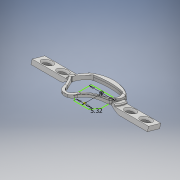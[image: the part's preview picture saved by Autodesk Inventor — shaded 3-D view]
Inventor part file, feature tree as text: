
AUTODESK INVENTOR PART (.ipt)
format: ipt  version: 2018 (Build 220112000, 112)  size: 2,529,280 bytes
history: native  units: mm
features: sketch x73, extrude x68, fillet x42, mirror x3, shell x1, hole x1
ambient origin geometry x8: Origin, YZ Plane, XZ Plane, XY Plane, X Axis, Y Axis, Z Axis, Center Point
bodies: Solid1 (feature_tree)
feature tree (188):
  extrude  "Extrusion1"  TaperAngle=0.0deg  [1 undecoded]
  extrude  "Extrusion2"  Depth=10.0mm
  extrude  "Extrusion3"  TaperAngle=0.0deg  [1 undecoded]
  shell  "Shell2"  Thickness=0.0mm
  extrude  "Extrusion4"  Depth=1.6mm
  extrude  "Extrusion6"  Depth=10.0mm TaperAngle=0.0deg
  extrude  "Extrusion7"  Depth=1.75mm
  extrude  "Extrusion8"  Depth=2.0mm
  extrude  "Extrusion9"  Depth=10.0mm TaperAngle=0.0deg
  extrude  "Extrusion11"  Depth=10.0mm TaperAngle=0.0deg
  fillet  "Fillet1"  Radius=10.0mm
  fillet  "Fillet2"  Radius=10.0mm
  fillet  "Fillet3"  [1 undecoded]
  fillet  "Fillet4"  Radius=0.541mm
  fillet  "Fillet5"  [1 undecoded]
  extrude  "Extrusion12"  Depth=7.5mm TaperAngle=0.0deg
  extrude  "Extrusion13"  TaperAngle=0.0deg  [1 undecoded]
  extrude  "Extrusion16"  Depth=51.0mm TaperAngle=0.0deg
  extrude  "Extrusion17"  TaperAngle=0.0deg  [1 undecoded]
  extrude  "Extrusion18"  Depth=10.0mm TaperAngle=0.0deg
  extrude  "Extrusion19"  Depth=10.0mm TaperAngle=0.0deg
  fillet  "Fillet6"  Radius=6.0mm
  extrude  "Extrusion20"  Depth=42.0mm TaperAngle=0.0deg
  fillet  "Fillet7"  Radius=42.0mm
  extrude  "Extrusion21"  Depth=2.6mm
  extrude  "Extrusion22"  Depth=2.6mm
  sketch  "Sketch23"  dims[d147=12.0125mm d148=12.0125mm]
  extrude  "Extrusion24"  Depth=12.0125mm
  extrude  "Extrusion26"  Depth=17.5mm
  extrude  "Extrusion28"  Depth=3.0mm
  extrude  "Extrusion32"  Depth=3.0mm
  extrude  "Extrusion37"  Depth=12.0mm TaperAngle=0.0deg
  extrude  "Extrusion38"  Depth=10.0mm TaperAngle=0.0deg
  extrude  "Extrusion40"  Depth=3.11mm
  extrude  "Extrusion41"  Depth=10.0mm TaperAngle=0.0deg
  extrude  "Extrusion42"  Depth=0.365mm TaperAngle=0.0deg
  extrude  "Extrusion43"  TaperAngle=0.0deg  [1 undecoded]
  extrude  "Extrusion44"  TaperAngle=0.0deg  [1 undecoded]
  hole  "Hole1"  [1 undecoded]
  sketch  "Sketch45"  dims[d203=20.0mm d204=15.65mm d205=0.0mm]
  extrude  "Extrusion45"  Depth=15.65mm TaperAngle=0.0deg
  extrude  "Extrusion47"  Depth=0.861mm
  mirror  "Mirror1"
  extrude  "Extrusion48"  Depth=1.61mm
  fillet  "Fillet23"  [1 undecoded]
  fillet  "Fillet24"  Radius=1.92mm
  extrude  "Extrusion49"  Depth=0.276mm
  extrude  "Extrusion50"  TaperAngle=0.0deg  [1 undecoded]
  extrude  "Extrusion54"  TaperAngle=0.0deg  [1 undecoded]
  extrude  "Extrusion55"  Depth=2.5mm
  extrude  "Extrusion56"  TaperAngle=0.0deg  [1 undecoded]
  extrude  "Extrusion57"  Depth=10.0mm TaperAngle=0.0deg
  sketch  "Sketch61"  dims[d255=2.57mm d256=2.37mm]
  extrude  "Extrusion58"  Depth=0.83mm TaperAngle=0.0deg
  extrude  "Extrusion59"  Depth=2.37mm
  extrude  "Extrusion60"  Depth=4.5mm
  fillet  "Fillet27"  Radius=0.83mm
  fillet  "Fillet28"  Radius=6.37mm
  extrude  "Extrusion61"  Depth=6.37mm TaperAngle=0.0deg
  fillet  "Fillet29"  Radius=6.71mm
  fillet  "Fillet30"  Radius=6.71mm
  fillet  "Fillet31"  [1 undecoded]
  fillet  "Fillet32"  Radius=2.0mm
  extrude  "Extrusion62"  Depth=2.0mm
  fillet  "Fillet33"  Radius=2.0mm
  fillet  "Fillet34"  Radius=2.0mm
  fillet  "Fillet35"  Radius=2.0mm
  fillet  "Fillet36"  Radius=2.0mm
  extrude  "Extrusion63"  Depth=1.9mm
  extrude  "Extrusion64"  Depth=0.616mm
  extrude  "Extrusion65"  Depth=2.0mm
  fillet  "Fillet37"  Radius=1.76mm
  fillet  "Fillet38"  [1 undecoded]
  extrude  "Extrusion69"  Depth=0.409mm
  extrude  "Extrusion70"  Depth=6.7mm TaperAngle=0.0deg
  extrude  "Extrusion71"  TaperAngle=0.0deg  [1 undecoded]
  extrude  "Extrusion72"  Depth=2.0mm
  extrude  "Extrusion73"  Depth=6.7mm TaperAngle=0.0deg
  extrude  "Extrusion74"  Depth=0.241mm
  fillet  "Fillet42"  Radius=5.47mm
  fillet  "Fillet43"  Radius=0.184mm
  extrude  "Extrusion75"  [1 undecoded]
  extrude  "Extrusion76"  [1 undecoded]
  mirror  "Mirror2"
  extrude  "Extrusion77"  [1 undecoded]
  extrude  "Extrusion78"  [1 undecoded]
  extrude  "Extrusion79"  [1 undecoded]
  mirror  "Mirror3"
  extrude  "Extrusion80"  [1 undecoded]
  extrude  "Extrusion81"  [1 undecoded]
  fillet  "Fillet44"  [1 undecoded]
  fillet  "Fillet45"  [1 undecoded]
  fillet  "Fillet46"  [1 undecoded]
  fillet  "Fillet47"  [1 undecoded]
  fillet  "Fillet48"  [1 undecoded]
  fillet  "Fillet49"  [1 undecoded]
  fillet  "Fillet50"  [1 undecoded]
  sketch  "Sketch86"
  fillet  "Fillet51"  [1 undecoded]
  fillet  "Fillet52"  [1 undecoded]
  fillet  "Fillet53"  [1 undecoded]
  fillet  "Fillet54"  [1 undecoded]
  sketch  "Sketch87"
  extrude  "Extrusion82"  [1 undecoded]
  extrude  "Extrusion83"  [1 undecoded]
  extrude  "Extrusion84"  [1 undecoded]
  fillet  "Fillet55"  [1 undecoded]
  fillet  "Fillet56"  [1 undecoded]
  extrude  "Extrusion85"  [1 undecoded]
  extrude  "Extrusion86"  [1 undecoded]
  extrude  "Extrusion87"  [1 undecoded]
  fillet  "Fillet57"  [1 undecoded]
  fillet  "Fillet58"  [1 undecoded]
  extrude  "Extrusion88"  [1 undecoded]
  extrude  "Extrusion89"  [1 undecoded]
  fillet  "Fillet59"  [1 undecoded]
  fillet  "Fillet60"  [1 undecoded]
  fillet  "Fillet61"  [1 undecoded]
  fillet  "Fillet62"  [1 undecoded]
  extrude  "Extrusion90"  [1 undecoded]
  sketch  "Sketch1"  dims[d0=10.0mm d1=0.0mm d4=0.0mm d5=0.0mm]
  sketch  "Sketch2"  dims[d6=10.0mm d7=0.0mm d9=1.2mm]
  sketch  "Sketch3"  dims[d10=0.0mm d11=0.0mm d14=0.0mm d15=0.0mm d16=0.0mm d17=0.0mm]
  sketch  "Sketch4"  dims[d18=0.0mm d19=0.0mm d20=1.6mm]
  sketch  "Sketch6"  dims[d21=0.0mm d22=0.0mm d25=10.0mm d26=0.0mm]
  sketch  "Sketch7"  dims[d27=2.23mm d28=1.75mm]
  sketch  "Sketch8"  dims[d29=2.79mm d30=2.0mm]
  sketch  "Sketch9"  dims[d31=5.19mm d32=10.0mm d33=0.0mm]
  sketch  "Sketch11"  dims[d34=10.0mm d35=0.0mm d40=10.0mm d41=0.0mm d42=10.0mm d43=0.0mm d44=10.0mm d45=0.0mm d46=0.0mm d47=0.0mm d48=0.541mm d49=0.0mm d50=0.0mm]
  sketch  "Sketch12"  dims[d51=4.84mm d52=7.5mm d53=0.0mm]
  sketch  "Sketch13"  dims[d54=0.0mm d55=0.0mm d59=0.0mm d60=0.0mm]
  sketch  "Sketch16"  dims[d78=51.0mm d79=0.0mm d84=51.0mm d85=0.0mm]
  sketch  "Sketch17"  dims[d94=51.0mm d95=0.0mm d123=0.0mm d124=0.0mm]
  sketch  "Sketch18"  dims[d125=0.0mm d126=0.0mm d131=10.0mm d132=0.0mm]
  sketch  "Sketch19"  dims[d133=10.0mm d134=0.0mm d135=10.0mm d136=0.0mm d137=6.0mm]
  sketch  "Sketch20"  dims[d138=1.9mm d139=42.0mm d140=0.0mm d141=42.0mm d142=0.0mm]
  sketch  "Sketch21"  dims[d143=2.6mm d144=2.6mm]
  sketch  "Sketch22"  dims[d145=2.6mm d146=2.6mm]
  sketch  "Sketch24"  dims[d149=17.5mm d150=17.5mm]
  sketch  "Sketch26"  dims[d151=3.0mm d152=3.0mm]
  sketch  "Sketch28"  dims[d153=3.0mm d154=3.0mm]
  sketch  "Sketch32"  dims[d155=2.6mm d156=6.0mm d157=4.4mm d158=2.0mm d159=14.3117mm d160=8.0mm d161=20.594885mm d162=12.0mm d163=0.0mm]
  sketch  "Sketch37"  dims[d170=10.0mm d171=0.0mm d172=10.0mm d173=0.0mm]
  sketch  "Sketch38"  dims[d174=3.64mm d175=3.11mm]
  sketch  "Sketch40"  dims[d176=0.0mm d177=0.0mm d178=10.0mm d179=0.0mm]
  sketch  "Sketch41"  dims[d186=0.365mm d187=0.0mm d190=0.365mm d191=0.0mm]
  sketch  "Sketch42"  dims[d192=0.0mm d193=0.0mm d194=0.0mm d195=0.0mm]
  sketch  "Sketch43"  dims[d196=0.0mm d197=0.0mm d198=0.0mm d199=0.0mm]
  sketch  "Sketch44"  dims[d200=0.0mm d201=0.0mm d202=2.0mm]
  sketch  "Sketch46"  dims[d206=0.675mm d207=0.861mm]
  sketch  "Sketch48"  dims[d208=0.8mm d209=1.61mm d210=0.0mm d211=0.0mm d212=1.92mm]
  sketch  "Sketch49"  dims[d213=2.91mm d214=0.276mm]
  sketch  "Sketch50"  dims[d215=0.425mm d218=0.0mm d219=0.0mm]
  sketch  "Sketch51"  dims[d222=10.0mm d223=0.0mm d226=0.0mm d227=0.0mm]
  sketch  "Sketch55"  dims[d228=5.04mm d229=2.5mm]
  sketch  "Sketch57"  dims[d241=10.0mm d242=0.0mm d245=0.0mm d246=0.0mm]
  sketch  "Sketch59"  dims[d247=10.0mm d248=0.0mm d249=1.22mm d250=0.0mm]
  sketch  "Sketch60"  dims[d251=0.0mm d252=0.0mm d253=0.83mm d254=0.0mm]
  sketch  "Sketch62"  dims[d257=9.0mm d258=5.320111mm d259=8.0mm d260=4.5mm d261=0.83mm d262=0.0mm d263=6.37mm d264=0.0mm]
  sketch  "Sketch63"  dims[d265=6.37mm d266=0.0mm d267=6.37mm d268=0.0mm d269=6.71mm d270=0.0mm d271=6.71mm d272=0.0mm d273=0.0mm d274=0.0mm d275=2.0mm]
  sketch  "Sketch64"  dims[d276=0.789mm d277=2.0mm d278=2.0mm d279=2.0mm d280=2.0mm d281=2.0mm]
  sketch  "Sketch65"  dims[d282=9.0mm d283=5.320111mm d284=8.0mm d285=1.9mm]
  sketch  "Sketch66"  dims[d286=0.3mm d287=0.616mm]
  sketch  "Sketch67"  dims[d288=2.0mm d289=2.0mm d290=1.76mm d291=0.0mm d292=0.0mm d293=0.0mm]
  sketch  "Sketch68"  dims[d294=0.6mm d295=0.0mm d296=0.409mm]
  sketch  "Sketch69"  dims[d297=0.323mm d298=6.7mm d299=0.0mm]
  sketch  "Sketch73"  dims[d300=6.7mm d301=0.0mm d302=0.0mm d303=0.0mm]
  sketch  "Sketch74"  dims[d304=2.0mm d305=2.0mm]
  sketch  "Sketch75"  dims[d306=0.0mm d307=0.0mm d308=6.7mm d309=0.0mm]
  sketch  "Sketch76"  dims[d310=2.0mm d311=0.241mm d312=5.47mm d313=0.184mm]
  sketch  "Sketch77"  dims[d314=0.0mm d315=0.0mm]
  sketch  "Sketch78"
  sketch  "Sketch79"
  sketch  "Sketch80"
  sketch  "Sketch81"
  sketch  "Sketch82"
  sketch  "Sketch83"
  sketch  "Sketch84"
  sketch  "Sketch85"
  sketch  "Sketch88"
  sketch  "Sketch89"
  sketch  "Sketch90"
  sketch  "Sketch91"
  sketch  "Sketch92"
  sketch  "Sketch93"
  sketch  "Sketch94"
  sketch  "Sketch95"
  sketch  "Sketch96"
note: 51 required parameter values undecoded (feature->parameter linkage not recoverable at this tier; creation-order binding heuristic only, values carry confidence <= 0.55)
